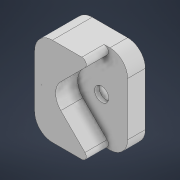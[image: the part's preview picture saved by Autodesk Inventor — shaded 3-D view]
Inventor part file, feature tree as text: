
AUTODESK INVENTOR PART (.ipt)
format: ipt  version: 2022 (Build 260153000, 153)  size: 233,984 bytes
history: native  units: mm
features: extrude x11, sketch x11, fillet x2
ambient origin geometry x8: Origin, YZ Plane, XZ Plane, XY Plane, X Axis, Y Axis, Z Axis, Center Point
bodies: Solid1 (feature_tree)
feature tree (24):
  extrude  "Extrusion1"  Depth=10.0mm
  extrude  "Extrusion2"  Depth=4.0mm
  extrude  "Extrusion3"  Depth=3.2mm
  extrude  "Extrusion5"  Depth=4.0mm TaperAngle=0.0deg
  extrude  "Extrusion6"  Depth=3.2mm
  extrude  "Extrusion8"  Depth=4.0mm
  extrude  "Extrusion9"  Depth=4.0mm
  extrude  "Extrusion10"  Depth=1.657mm
  extrude  "Extrusion11"  TaperAngle=45.0deg  [1 undecoded]
  extrude  "Extrusion12"  Depth=5.0mm TaperAngle=0.0deg
  extrude  "Extrusion13"  Depth=4.0mm
  fillet  "Fillet2"  Radius=5.9mm
  fillet  "Fillet3"  Radius=3.0mm
  sketch  "Sketch1"  dims[d0=20.0mm d1=10.0mm]
  sketch  "Sketch2"  dims[d2=4.0mm d3=0.0mm d4=7.071mm]
  sketch  "Sketch3"  dims[d5=7.071mm d6=3.2mm]
  sketch  "Sketch5"  dims[d7=5.9mm d8=4.0mm d9=0.0mm]
  sketch  "Sketch6"  dims[d10=7.071mm d11=3.2mm]
  sketch  "Sketch8"  dims[d12=3.0mm d13=0.0mm d17=4.0mm]
  sketch  "Sketch9"  dims[d18=4.0mm d19=0.0mm d21=4.0mm]
  sketch  "Sketch10"  dims[d22=45.0deg d24=1.657mm]
  sketch  "Sketch11"  dims[d25=45.0deg d26=45.0deg]
  sketch  "Sketch12"  dims[d27=4.0mm d28=5.0mm d29=0.0mm]
  sketch  "Sketch13"  dims[d35=45.0deg d36=4.0mm d37=5.9mm d38=3.0mm d39=0.0mm d40=5.9mm d41=3.9mm d42=0.0mm d43=5.1mm d44=0.0mm d45=5.0mm d46=0.0mm d47=5.0mm d48=0.0mm d50=45.0deg d51=45.0deg d52=5.0mm d53=0.0mm d54=4.0mm d55=1.0mm]
note: 1 required parameter value undecoded (feature->parameter linkage not recoverable at this tier; creation-order binding heuristic only, values carry confidence <= 0.55)
